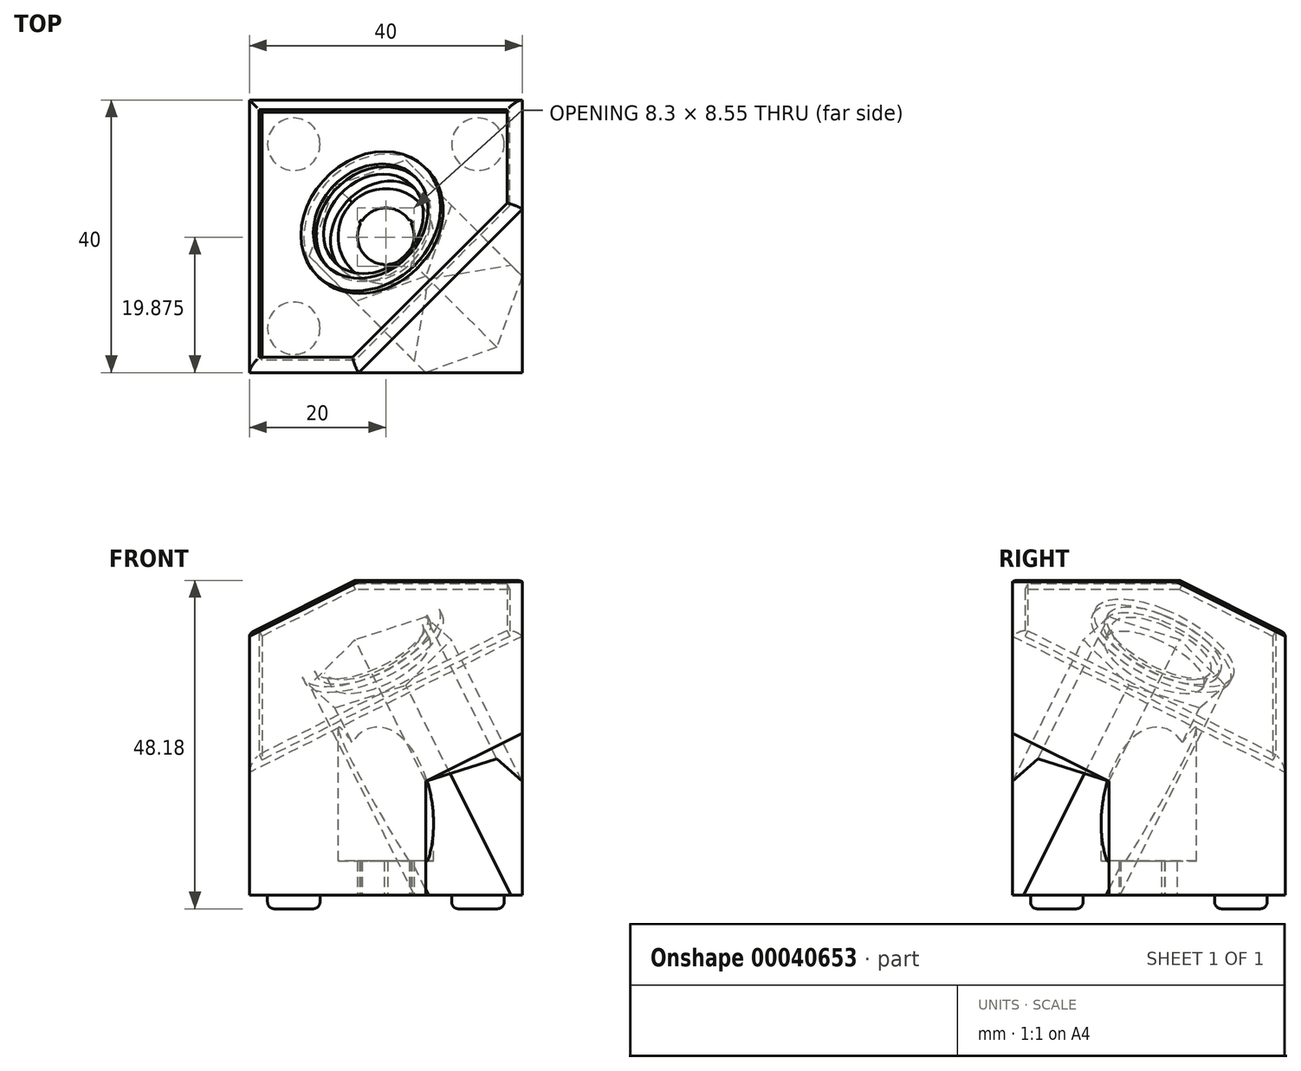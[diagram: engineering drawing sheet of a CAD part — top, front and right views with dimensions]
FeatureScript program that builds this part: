
annotation { "Feature Type Name" : "Feature", "Feature Type Description" : "" }
export const myFeature = defineFeature(function(context is Context, id is Id, definition is map)
    precondition{}
    {
        {
            var Q0;
            Q0=qCreatedBy(makeId("Top.planeOp"),FACE);
            var sketch = newSketch(context, id + "F0", { "sketchPlane" : qUnion([Q0])});
            skLineSegment(sketch, "E0.bottom", {"start": v(20, -20) * mm, "end": v(-20, -20) * mm});
            skLineSegment(sketch, "E0.top", {"start": v(20, 20) * mm, "end": v(-20, 20) * mm});
            skLineSegment(sketch, "E0.left", {"start": v(20, -20) * mm, "end": v(20, 20) * mm});
            skLineSegment(sketch, "E0.right", {"start": v(-20, -20) * mm, "end": v(-20, 20) * mm});
            skPoint(sketch, "E0.middle", {"position": v(0, 0) * mm});
            skSolve(sketch);
        }
        {
            var Q0;
            Q0=makeQuery(id+"F0.imprint","IMPRINT",FACE,{"disambiguationData":[TD([[makeQuery(id+"F0.imprint","IMPRINT",EDGE,{"derivedFrom":sQuery(id+"F0.wireOp",EDGE,"E0.bottom")}),-1.0]])]});
            extrude(context, id + "F1", {"entities" : qUnion([Q0]), "depth" : 20 * mm});
        }
        {
            var Q0;
            Q0=makeQuery(id+"F1.opExtrude","CAP_VERTEX",VERTEX,{"disambiguationData":[OSD([sQuery(id+"F0.wireOp",EDGE,"E0.top"),sQuery(id+"F0.wireOp",EDGE,"E0.left")])],"isStart":false});
            var Q1;
            Q1=makeQuery(id+"F1.opExtrude","CAP_VERTEX",VERTEX,{"disambiguationData":[OSD([sQuery(id+"F0.wireOp",EDGE,"E0.bottom"),sQuery(id+"F0.wireOp",EDGE,"E0.right")])],"isStart":false});
            var Q2;
            Q2=makeQuery(id+"F1.opExtrude","CAP_VERTEX",VERTEX,{"disambiguationData":[OSD([sQuery(id+"F0.wireOp",EDGE,"E0.top"),sQuery(id+"F0.wireOp",EDGE,"E0.right")])],"isStart":true});
            cPlane(context, id + "F2", {"entities" : qUnion([Q0, Q1, Q2]), "cplaneType" : CPlaneType.THREE_POINT, "offset" : 25 * mm, "width" : 150 * mm, "height" : 150 * mm});
        }
        {
            var Q0;
            Q0=makeQuery(id+"F1.opExtrude","CAP_FACE",FACE,{"disambiguationData":[OSD([sQuery(id+"F0.wireOp",EDGE,"E0.bottom"),sQuery(id+"F0.wireOp",EDGE,"E0.top"),sQuery(id+"F0.wireOp",EDGE,"E0.left"),sQuery(id+"F0.wireOp",EDGE,"E0.right")])],"isStart":true});
            extrude(context, id + "F3", {"entities" : qUnion([Q0]), "operationType" : NewBodyOperationType.ADD, "depth" : 18 * mm});
        }
        {
            var Q0;
            Q0=makeQuery(id+"F1.opExtrude","CAP_FACE",FACE,{"disambiguationData":[OSD([sQuery(id+"F0.wireOp",EDGE,"E0.bottom"),sQuery(id+"F0.wireOp",EDGE,"E0.top"),sQuery(id+"F0.wireOp",EDGE,"E0.left"),sQuery(id+"F0.wireOp",EDGE,"E0.right")])],"isStart":false});
            extrude(context, id + "F4", {"entities" : qUnion([Q0]), "operationType" : NewBodyOperationType.ADD, "depth" : 8 * mm});
        }
        {
            var Q0;
            Q0=qCreatedBy(id+"F2.planeOp",FACE);
            var sketch = newSketch(context, id + "F5", { "sketchPlane" : qUnion([Q0])});
            skCircle(sketch, "E1", {"center": v(2.39, -7.49) * mm, "radius": 48.4 * mm});
            skSolve(sketch);
        }
        {
            var Q0;
            Q0=makeQuery(id+"F5.imprint","IMPRINT",FACE,{"disambiguationData":[TD([[makeQuery(id+"F5.imprint","IMPRINT",EDGE,{"derivedFrom":sQuery(id+"F5.wireOp",EDGE,"E1")}),1.0]])]});
            extrude(context, id + "F6", {"entities" : qUnion([Q0]), "operationType" : NewBodyOperationType.REMOVE, "depth" : 25 * mm});
        }
        {
            var Q0;
            Q0=makeQuery(id+"F6.boolean.opBoolean","COPY",FACE,{"derivedFrom":makeQuery(id+"F6.opExtrude","CAP_FACE",FACE,{"disambiguationData":[OSD([sQuery(id+"F5.wireOp",EDGE,"E1")])],"isStart":true})});
            var sketch = newSketch(context, id + "F7", { "sketchPlane" : qUnion([Q0])});
            skLineSegment(sketch, "E2", {"start": v(16.07, -19.68) * mm, "end": v(-14.6, 17.89) * mm, "construction": true});
            skCircle(sketch, "E3", {"center": v(5.31, -6.5) * mm, "radius": 8 * mm});
            skSolve(sketch);
        }
        {
            var Q0;
            Q0=makeQuery(id+"F7.imprint","IMPRINT",FACE,{"disambiguationData":[TD([[makeQuery(id+"F7.imprint","IMPRINT",EDGE,{"derivedFrom":sQuery(id+"F7.wireOp",EDGE,"E3")}),1.0]])]});
            extrude(context, id + "F8", {"entities" : qUnion([Q0]), "operationType" : NewBodyOperationType.REMOVE, "endBound" : BoundingType.THROUGH_ALL, "oppositeDirection" : true, "depth" : 25 * mm});
        }
        {
            var Q0;
            Q0=qCreatedBy(id+"F2.planeOp",FACE);
            cPlane(context, id + "F9", {"entities" : qUnion([Q0]), "cplaneType" : CPlaneType.OFFSET, "offset" : 40 * mm, "oppositeDirection" : true, "width" : 150 * mm, "height" : 150 * mm});
        }
        {
            var Q0;
            Q0=qCreatedBy(id+"F9.planeOp",FACE);
            var sketch = newSketch(context, id + "F10", { "sketchPlane" : qUnion([Q0])});
            skArc(sketch, "E4.0", {"start": v(10.03, -0.05) * mm, "mid": v(0.26, -0.31) * mm, "end": v(-1.96, -9.84) * mm, "construction": true});
            skArc(sketch, "E5.0", {"start": v(10.37, -12.7) * mm, "mid": v(3.5, -14.3) * mm, "end": v(-1.96, -9.84) * mm, "construction": true});
            skArc(sketch, "E6.0", {"start": v(10.37, -12.7) * mm, "mid": v(13.31, -6.3) * mm, "end": v(10.03, -0.05) * mm, "construction": true});
            skCircle(sketch, "E7.cCircle", {"center": v(5.31, -6.5) * mm, "radius": 10 * mm, "construction": true});
            skLineSegment(sketch, "E7.0", {"start": v(9.4, 4.29) * mm, "end": v(16.71, -4.66) * mm});
            skLineSegment(sketch, "E7.1", {"start": v(16.71, -4.66) * mm, "end": v(12.62, -15.45) * mm});
            skLineSegment(sketch, "E7.2", {"start": v(12.62, -15.45) * mm, "end": v(1.22, -17.3) * mm});
            skLineSegment(sketch, "E7.3", {"start": v(1.22, -17.3) * mm, "end": v(-6.08, -8.36) * mm});
            skLineSegment(sketch, "E7.4", {"start": v(-6.08, -8.36) * mm, "end": v(-1.99, 2.44) * mm});
            skLineSegment(sketch, "E7.5", {"start": v(-1.99, 2.44) * mm, "end": v(9.4, 4.29) * mm});
            skPoint(sketch, "E7.0.midPoint", {"position": v(13.06, -0.18) * mm});
            skLineSegment(sketch, "E8.0", {"start": v(24.83, -30.41) * mm, "end": v(10.37, -12.7) * mm, "construction": true});
            skLineSegment(sketch, "E9", {"start": v(-18.46, -33.37) * mm, "end": v(44.1, 17.7) * mm});
            skLineSegment(sketch, "E10", {"start": v(44.1, 17.7) * mm, "end": v(61.04, -3.05) * mm});
            skLineSegment(sketch, "E11", {"start": v(61.04, -3.05) * mm, "end": v(-1.51, -54.13) * mm});
            skLineSegment(sketch, "E12", {"start": v(-1.51, -54.13) * mm, "end": v(-18.46, -33.37) * mm});
            skSolve(sketch);
        }
        {
            var Q0;
            Q0=makeQuery(id+"F10.imprint","IMPRINT",FACE,{"disambiguationData":[TD([[makeQuery(id+"F10.imprint","IMPRINT",EDGE,{"derivedFrom":sQuery(id+"F10.wireOp",EDGE,"E7.0")}),-1.0]])]});
            var Q1;
            {var subQ0=sQuery(id+"F10.wireOp",EDGE,"E7.2");Q1=makeQuery(id+"F10.imprint","IMPRINT",FACE,{"disambiguationData":[TD([[makeQuery(id+"F10.imprint","IMPRINT",EDGE,{"derivedFrom":subQ0}),-1.0]])]});}
            extrude(context, id + "F11", {"entities" : qUnion([Q0, Q1]), "operationType" : NewBodyOperationType.REMOVE, "oppositeDirection" : true, "depth" : 75 * mm, "symmetric" : true});
        }
        {
            var Q0;
            {var subQ1=sQuery(id+"F10.wireOp",EDGE,"E7.1");Q0=makeQuery(id+"F10.imprint","IMPRINT",FACE,{"disambiguationData":[TD([[makeQuery(id+"F10.imprint","IMPRINT",EDGE,{"derivedFrom":subQ1}),1.0]])]});}
            extrude(context, id + "F12", {"entities" : qUnion([Q0]), "operationType" : NewBodyOperationType.REMOVE, "depth" : 12.05 * mm});
        }
        {
            var Q0;
            Q0=makeQuery(id+"F3.opExtrude","CAP_FACE",FACE,{"disambiguationData":[OSD([sQuery(id+"F0.wireOp",EDGE,"E0.bottom"),sQuery(id+"F0.wireOp",EDGE,"E0.top"),sQuery(id+"F0.wireOp",EDGE,"E0.left"),sQuery(id+"F0.wireOp",EDGE,"E0.right")])],"isStart":false});
            var sketch = newSketch(context, id + "F13", { "sketchPlane" : qUnion([Q0])});
            skArc(sketch, "E13", {"start": v(-0.25, 4.14) * mm, "mid": v(-3.6, 2.08) * mm, "end": v(-3.71, -1.85) * mm});
            skArc(sketch, "E14", {"start": v(0.25, 4.14) * mm, "mid": v(0, 4.4) * mm, "end": v(-0.25, 4.14) * mm});
            skArc(sketch, "E15.1.0", {"start": v(-3.71, -1.85) * mm, "mid": v(-3.81, -2.2) * mm, "end": v(-3.46, -2.29) * mm});
            skArc(sketch, "E15.2.0", {"start": v(3.46, -2.29) * mm, "mid": v(3.81, -2.2) * mm, "end": v(3.71, -1.85) * mm});
            skArc(sketch, "E16.trimOffspring", {"start": v(3.71, -1.85) * mm, "mid": v(3.6, 2.08) * mm, "end": v(0.25, 4.14) * mm});
            skArc(sketch, "E17.trimOffspring", {"start": v(-3.46, -2.29) * mm, "mid": v(0, -4.15) * mm, "end": v(3.46, -2.29) * mm});
            skCircle(sketch, "E18", {"center": v(-13.5, 13.5) * mm, "radius": 3.85 * mm});
            skCircle(sketch, "E19.1.0", {"center": v(-13.5, -13.5) * mm, "radius": 3.85 * mm});
            skCircle(sketch, "E19.2.0", {"center": v(13.5, -13.5) * mm, "radius": 3.85 * mm});
            skCircle(sketch, "E19.3.0", {"center": v(13.5, 13.5) * mm, "radius": 3.85 * mm});
            skLineSegment(sketch, "E20.rect.bottom", {"start": v(19, -20) * mm, "end": v(-19, -20) * mm});
            skLineSegment(sketch, "E20.rect.top", {"start": v(19, 20) * mm, "end": v(4.2, 20) * mm});
            skLineSegment(sketch, "E20.rect.left", {"start": v(20, -19) * mm, "end": v(20, 19) * mm});
            skLineSegment(sketch, "E20.rect.right", {"start": v(-20, -19) * mm, "end": v(-20, 19) * mm});
            skPoint(sketch, "E21.visualSharp", {"position": v(-20, 20) * mm});
            skArc(sketch, "E21.filletArc", {"start": v(-19, 20) * mm, "mid": v(-19.7, 19.7) * mm, "end": v(-20, 19) * mm});
            skPoint(sketch, "E22.visualSharp", {"position": v(20, 20) * mm});
            skArc(sketch, "E22.filletArc", {"start": v(20, 19) * mm, "mid": v(19.7, 19.7) * mm, "end": v(19, 20) * mm});
            skPoint(sketch, "E23.visualSharp", {"position": v(-20, -20) * mm});
            skArc(sketch, "E23.filletArc", {"start": v(-20, -19) * mm, "mid": v(-19.7, -19.7) * mm, "end": v(-19, -20) * mm});
            skPoint(sketch, "E24.visualSharp", {"position": v(20, -20) * mm});
            skArc(sketch, "E24.filletArc", {"start": v(19, -20) * mm, "mid": v(19.7, -19.7) * mm, "end": v(20, -19) * mm});
            skLineSegment(sketch, "E25.rect.bottom", {"start": v(-16, -4.2) * mm, "end": v(-20, -4.2) * mm});
            skLineSegment(sketch, "E25.rect.top", {"start": v(-16, 4.2) * mm, "end": v(-20, 4.2) * mm});
            skLineSegment(sketch, "E25.rect.right", {"start": v(-20, -4.2) * mm, "end": v(-20, 4.2) * mm});
            skPoint(sketch, "E25.rect.middle", {"position": v(-18, 0) * mm});
            skLineSegment(sketch, "E26.rect.bottom", {"start": v(-16, 7.25) * mm, "end": v(-9.36, 7.25) * mm});
            skLineSegment(sketch, "E26.rect.top", {"start": v(-16, -7.25) * mm, "end": v(-9.36, -7.25) * mm});
            skLineSegment(sketch, "E26.rect.left", {"start": v(-16, 7.25) * mm, "end": v(-16, 4.2) * mm});
            skPoint(sketch, "E26.rect.middle", {"position": v(-12.68, 0) * mm});
            skPoint(sketch, "E26.rect.middle.positionSnap0", {"position": v(-16, 0) * mm});
            skPoint(sketch, "E26.rect.cornerSnap0", {"position": v(-16, 0) * mm});
            skPoint(sketch, "E26.rect.centerSnap0", {"position": v(-16, 0) * mm});
            skLineSegment(sketch, "E27.trimOffspring", {"start": v(-16, -4.2) * mm, "end": v(-16, -7.25) * mm});
            skArc(sketch, "E28", {"start": v(-9.36, 7.25) * mm, "mid": v(-6, 0) * mm, "end": v(-9.36, -7.25) * mm});
            skLineSegment(sketch, "E29.1.0", {"start": v(4.2, -16) * mm, "end": v(7.25, -16) * mm});
            skLineSegment(sketch, "E29.1.1", {"start": v(4.2, -16) * mm, "end": v(4.2, -20) * mm});
            skPoint(sketch, "E29.1.2", {"position": v(0, -16) * mm});
            skLineSegment(sketch, "E29.1.3", {"start": v(-7.25, -16) * mm, "end": v(-4.2, -16) * mm});
            skPoint(sketch, "E29.1.4", {"position": v(0, -18) * mm});
            skLineSegment(sketch, "E29.1.5", {"start": v(7.25, -16) * mm, "end": v(7.25, -9.36) * mm});
            skArc(sketch, "E29.1.6", {"start": v(-7.25, -9.36) * mm, "mid": v(0, -6) * mm, "end": v(7.25, -9.36) * mm});
            skLineSegment(sketch, "E29.1.7", {"start": v(-7.25, -16) * mm, "end": v(-7.25, -9.36) * mm});
            skLineSegment(sketch, "E29.1.8", {"start": v(4.2, -20) * mm, "end": v(-4.2, -20) * mm});
            skLineSegment(sketch, "E29.1.9", {"start": v(-4.2, -16) * mm, "end": v(-4.2, -20) * mm});
            skPoint(sketch, "E29.1.10", {"position": v(0, -12.68) * mm});
            skPoint(sketch, "E29.1.11", {"position": v(0, -16) * mm});
            skPoint(sketch, "E29.1.12", {"position": v(0, -16) * mm});
            skLineSegment(sketch, "E29.2.0", {"start": v(16, 4.2) * mm, "end": v(16, 7.25) * mm});
            skLineSegment(sketch, "E29.2.1", {"start": v(16, 4.2) * mm, "end": v(20, 4.2) * mm});
            skPoint(sketch, "E29.2.2", {"position": v(16, 0) * mm});
            skLineSegment(sketch, "E29.2.3", {"start": v(16, -7.25) * mm, "end": v(16, -4.2) * mm});
            skPoint(sketch, "E29.2.4", {"position": v(18, 0) * mm});
            skLineSegment(sketch, "E29.2.5", {"start": v(16, 7.25) * mm, "end": v(9.36, 7.25) * mm});
            skArc(sketch, "E29.2.6", {"start": v(9.36, -7.25) * mm, "mid": v(6, 0) * mm, "end": v(9.36, 7.25) * mm});
            skLineSegment(sketch, "E29.2.7", {"start": v(16, -7.25) * mm, "end": v(9.36, -7.25) * mm});
            skLineSegment(sketch, "E29.2.8", {"start": v(20, 4.2) * mm, "end": v(20, -4.2) * mm});
            skLineSegment(sketch, "E29.2.9", {"start": v(16, -4.2) * mm, "end": v(20, -4.2) * mm});
            skPoint(sketch, "E29.2.10", {"position": v(12.68, 0) * mm});
            skPoint(sketch, "E29.2.11", {"position": v(16, 0) * mm});
            skPoint(sketch, "E29.2.12", {"position": v(16, 0) * mm});
            skLineSegment(sketch, "E29.3.0", {"start": v(-4.2, 16) * mm, "end": v(-7.25, 16) * mm});
            skLineSegment(sketch, "E29.3.1", {"start": v(-4.2, 16) * mm, "end": v(-4.2, 20) * mm});
            skPoint(sketch, "E29.3.2", {"position": v(0, 16) * mm});
            skLineSegment(sketch, "E29.3.3", {"start": v(7.25, 16) * mm, "end": v(4.2, 16) * mm});
            skPoint(sketch, "E29.3.4", {"position": v(0, 18) * mm});
            skLineSegment(sketch, "E29.3.5", {"start": v(-7.25, 16) * mm, "end": v(-7.25, 9.36) * mm});
            skArc(sketch, "E29.3.6", {"start": v(7.25, 9.36) * mm, "mid": v(0, 6) * mm, "end": v(-7.25, 9.36) * mm});
            skLineSegment(sketch, "E29.3.7", {"start": v(7.25, 16) * mm, "end": v(7.25, 9.36) * mm});
            skLineSegment(sketch, "E29.3.8", {"start": v(-4.2, 20) * mm, "end": v(4.2, 20) * mm});
            skLineSegment(sketch, "E29.3.9", {"start": v(4.2, 16) * mm, "end": v(4.2, 20) * mm});
            skPoint(sketch, "E29.3.10", {"position": v(0, 12.68) * mm});
            skPoint(sketch, "E29.3.11", {"position": v(0, 16) * mm});
            skPoint(sketch, "E29.3.12", {"position": v(0, 16) * mm});
            skLineSegment(sketch, "E30.trimOffspring", {"start": v(-4.2, 20) * mm, "end": v(-19, 20) * mm});
            skSolve(sketch);
        }
        {
            var Q0;
            Q0=makeQuery(id+"F13.imprint","IMPRINT",FACE,{"disambiguationData":[TD([[makeQuery(id+"F13.imprint","IMPRINT",EDGE,{"derivedFrom":sQuery(id+"F13.wireOp",EDGE,"E18")}),1.0]])]});
            var Q1;
            Q1=makeQuery(id+"F13.imprint","IMPRINT",FACE,{"disambiguationData":[TD([[makeQuery(id+"F13.imprint","IMPRINT",EDGE,{"derivedFrom":sQuery(id+"F13.wireOp",EDGE,"E19.1.0")}),1.0]])]});
            var Q2;
            Q2=makeQuery(id+"F13.imprint","IMPRINT",FACE,{"disambiguationData":[TD([[makeQuery(id+"F13.imprint","IMPRINT",EDGE,{"derivedFrom":sQuery(id+"F13.wireOp",EDGE,"E19.2.0")}),1.0]])]});
            extrude(context, id + "F14", {"entities" : qUnion([Q0, Q1, Q2]), "operationType" : NewBodyOperationType.ADD, "depth" : 2 * mm});
        }
        {
            var Q0;
            Q0=makeQuery(id+"F13.imprint","IMPRINT",FACE,{"disambiguationData":[TD([[makeQuery(id+"F13.imprint","IMPRINT",EDGE,{"derivedFrom":sQuery(id+"F13.wireOp",EDGE,"E13")}),1.0]])]});
            extrude(context, id + "F15", {"entities" : qUnion([Q0]), "operationType" : NewBodyOperationType.REMOVE, "oppositeDirection" : true, "depth" : 25 * mm});
        }
        {
            var Q0;
            Q0=qCreatedBy(makeId("Top.planeOp"),FACE);
            var sketch = newSketch(context, id + "F16", { "sketchPlane" : qUnion([Q0])});
            skCircle(sketch, "E31", {"center": v(0, 0) * mm, "radius": 7 * mm});
            skSolve(sketch);
        }
        {
            var Q0;
            Q0=makeQuery(id+"F16.imprint","IMPRINT",FACE,{"disambiguationData":[TD([[makeQuery(id+"F16.imprint","IMPRINT",EDGE,{"derivedFrom":sQuery(id+"F16.wireOp",EDGE,"E31")}),1.0]])]});
            extrude(context, id + "F17", {"entities" : qUnion([Q0]), "operationType" : NewBodyOperationType.REMOVE, "oppositeDirection" : true, "depth" : 13 * mm});
        }
        {
            var Q0;
            Q0=makeQuery(id+"F16.imprint","IMPRINT",FACE,{"disambiguationData":[TD([[makeQuery(id+"F16.imprint","IMPRINT",EDGE,{"derivedFrom":sQuery(id+"F16.wireOp",EDGE,"E31")}),1.0]])]});
            extrude(context, id + "F18", {"entities" : qUnion([Q0]), "operationType" : NewBodyOperationType.REMOVE, "depth" : 18.5 * mm});
        }
        {
            var Q0;
            Q0=makeQuery(id+"F14.opExtrude","CAP_EDGE",EDGE,{"disambiguationData":[OSD([sQuery(id+"F13.wireOp",EDGE,"E19.1.0")])],"isStart":false});
            var Q1;
            Q1=makeQuery(id+"F14.opExtrude","CAP_EDGE",EDGE,{"disambiguationData":[OSD([sQuery(id+"F13.wireOp",EDGE,"E18")])],"isStart":false});
            var Q2;
            Q2=makeQuery(id+"F14.opExtrude","CAP_EDGE",EDGE,{"disambiguationData":[OSD([sQuery(id+"F13.wireOp",EDGE,"E19.2.0")])],"isStart":false});
            fillet(context, id + "F19", {"entities" : qUnion([Q0, Q1, Q2]), "radius" : 1 * mm, "tangentPropagation" : true, "allowEdgeOverflow" : false});
        }
        {
            var Q0;
            Q0=makeQuery(id+"F6.boolean.opBoolean","COPY",FACE,{"derivedFrom":makeQuery(id+"F6.opExtrude","CAP_FACE",FACE,{"disambiguationData":[OSD([sQuery(id+"F5.wireOp",EDGE,"E1")])],"isStart":true})});
            var sketch = newSketch(context, id + "F20", { "sketchPlane" : qUnion([Q0])});
            skLineSegment(sketch, "E32.0", {"start": v(29.21, -8.94) * mm, "end": v(29.21, 8.94) * mm});
            skLineSegment(sketch, "E33.0", {"start": v(29.21, -8.94) * mm, "end": v(2.92, -30.41) * mm});
            skLineSegment(sketch, "E34.0", {"start": v(2.92, -30.41) * mm, "end": v(-14.6, -26.83) * mm});
            skLineSegment(sketch, "E35.0", {"start": v(-14.6, -26.83) * mm, "end": v(-14.6, 17.89) * mm});
            skLineSegment(sketch, "E36.0", {"start": v(29.21, 8.94) * mm, "end": v(-14.6, 17.89) * mm});
            skLineSegment(sketch, "E37.0", {"start": v(2.4, -28.26) * mm, "end": v(-12.6, -25.2) * mm});
            skLineSegment(sketch, "E37.1", {"start": v(27.21, -8) * mm, "end": v(2.4, -28.26) * mm});
            skLineSegment(sketch, "E37.2", {"start": v(-12.6, -25.2) * mm, "end": v(-12.6, 15.44) * mm});
            skLineSegment(sketch, "E37.3", {"start": v(27.21, 7.31) * mm, "end": v(-12.6, 15.44) * mm});
            skLineSegment(sketch, "E37.4", {"start": v(27.21, -8) * mm, "end": v(27.21, 7.31) * mm});
            skCircle(sketch, "E38", {"center": v(5.31, -6.5) * mm, "radius": 9.2 * mm});
            skCircle(sketch, "E39.0", {"center": v(5.31, -6.5) * mm, "radius": 11.2 * mm});
            skSolve(sketch);
        }
        {
            var Q0;
            Q0=makeQuery(id+"F20.imprint","IMPRINT",FACE,{"disambiguationData":[TD([[makeQuery(id+"F20.imprint","IMPRINT",EDGE,{"derivedFrom":sQuery(id+"F20.wireOp",EDGE,"E32.0")}),1.0]])]});
            var Q1;
            Q1=makeQuery(id+"F20.imprint","IMPRINT",FACE,{"disambiguationData":[TD([[makeQuery(id+"F20.imprint","IMPRINT",EDGE,{"derivedFrom":sQuery(id+"F20.wireOp",EDGE,"E38")}),-1.0]])]});
            extrude(context, id + "F21", {"entities" : qUnion([Q0, Q1]), "operationType" : NewBodyOperationType.ADD, "depth" : 1 * mm});
        }
        {
            var Q0;
            Q0=makeQuery(id+"F21.opExtrude","CAP_EDGE",EDGE,{"disambiguationData":[OSD([sQuery(id+"F20.wireOp",EDGE,"E34.0")])],"isStart":false});
            var Q1;
            Q1=makeQuery(id+"F21.opExtrude","CAP_EDGE",EDGE,{"disambiguationData":[OSD([sQuery(id+"F20.wireOp",EDGE,"E35.0")])],"isStart":false});
            var Q2;
            Q2=makeQuery(id+"F21.opExtrude","CAP_EDGE",EDGE,{"disambiguationData":[OSD([sQuery(id+"F20.wireOp",EDGE,"E36.0")])],"isStart":false});
            var Q3;
            Q3=makeQuery(id+"F21.opExtrude","CAP_EDGE",EDGE,{"disambiguationData":[OSD([sQuery(id+"F20.wireOp",EDGE,"E32.0")])],"isStart":false});
            var Q4;
            Q4=makeQuery(id+"F21.opExtrude","CAP_EDGE",EDGE,{"disambiguationData":[OSD([sQuery(id+"F20.wireOp",EDGE,"E33.0")])],"isStart":false});
            fillet(context, id + "F22", {"entities" : qUnion([Q0, Q1, Q2, Q3, Q4]), "radius" : 2 * mm, "tangentPropagation" : true, "allowEdgeOverflow" : false});
        }
    });
